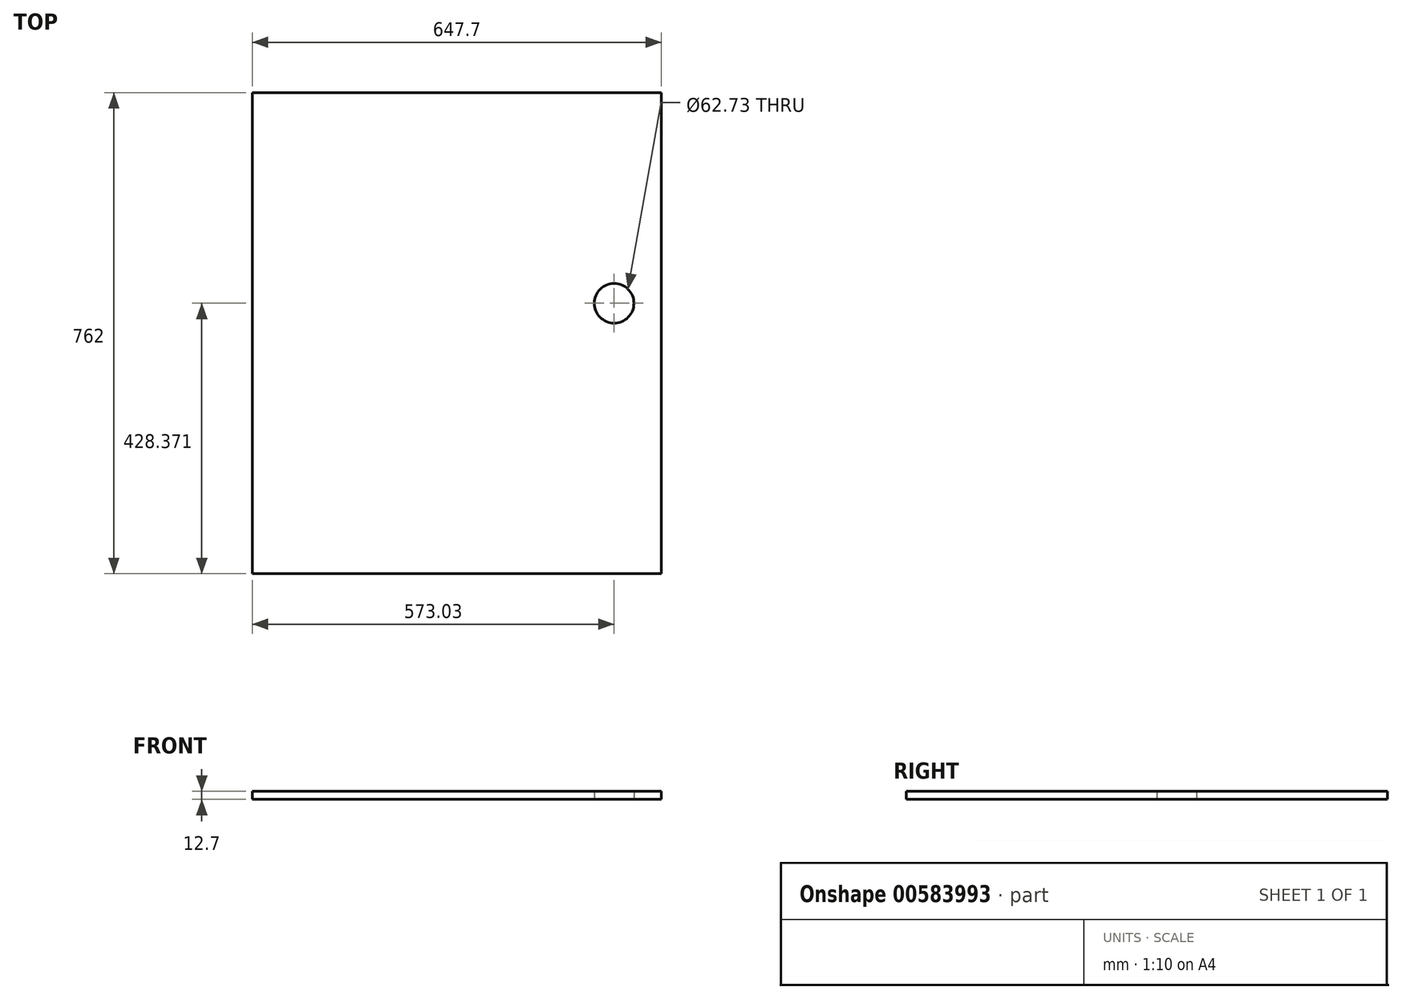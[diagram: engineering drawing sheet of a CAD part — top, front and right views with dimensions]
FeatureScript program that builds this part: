
annotation { "Feature Type Name" : "Feature", "Feature Type Description" : "" }
export const myFeature = defineFeature(function(context is Context, id is Id, definition is map)
    precondition{}
    {
        {
            var Q0;
            Q0=qCreatedBy(makeId("Top.planeOp"),FACE);
            var sketch = newSketch(context, id + "F0", { "sketchPlane" : qUnion([Q0])});
            skLineSegment(sketch, "E0.bottom", {"start": v(-472.4, 396.37) * mm, "end": v(175.3, 396.37) * mm});
            skLineSegment(sketch, "E0.top", {"start": v(-472.4, -365.63) * mm, "end": v(175.3, -365.63) * mm});
            skLineSegment(sketch, "E0.left", {"start": v(-472.4, 396.37) * mm, "end": v(-472.4, -365.63) * mm});
            skLineSegment(sketch, "E0.right", {"start": v(175.3, 396.37) * mm, "end": v(175.3, -365.63) * mm});
            skCircle(sketch, "E1", {"center": v(100.62, 62.74) * mm, "radius": 31.37 * mm});
            skSolve(sketch);
        }
        {
            var Q0;
            Q0=qSketchRegion(id+"F0",true);
            extrude(context, id + "F1", {"entities" : qUnion([Q0]), "depth" : 12.7 * mm, "offsetDistance" : 25.4 * mm});
        }
    });
